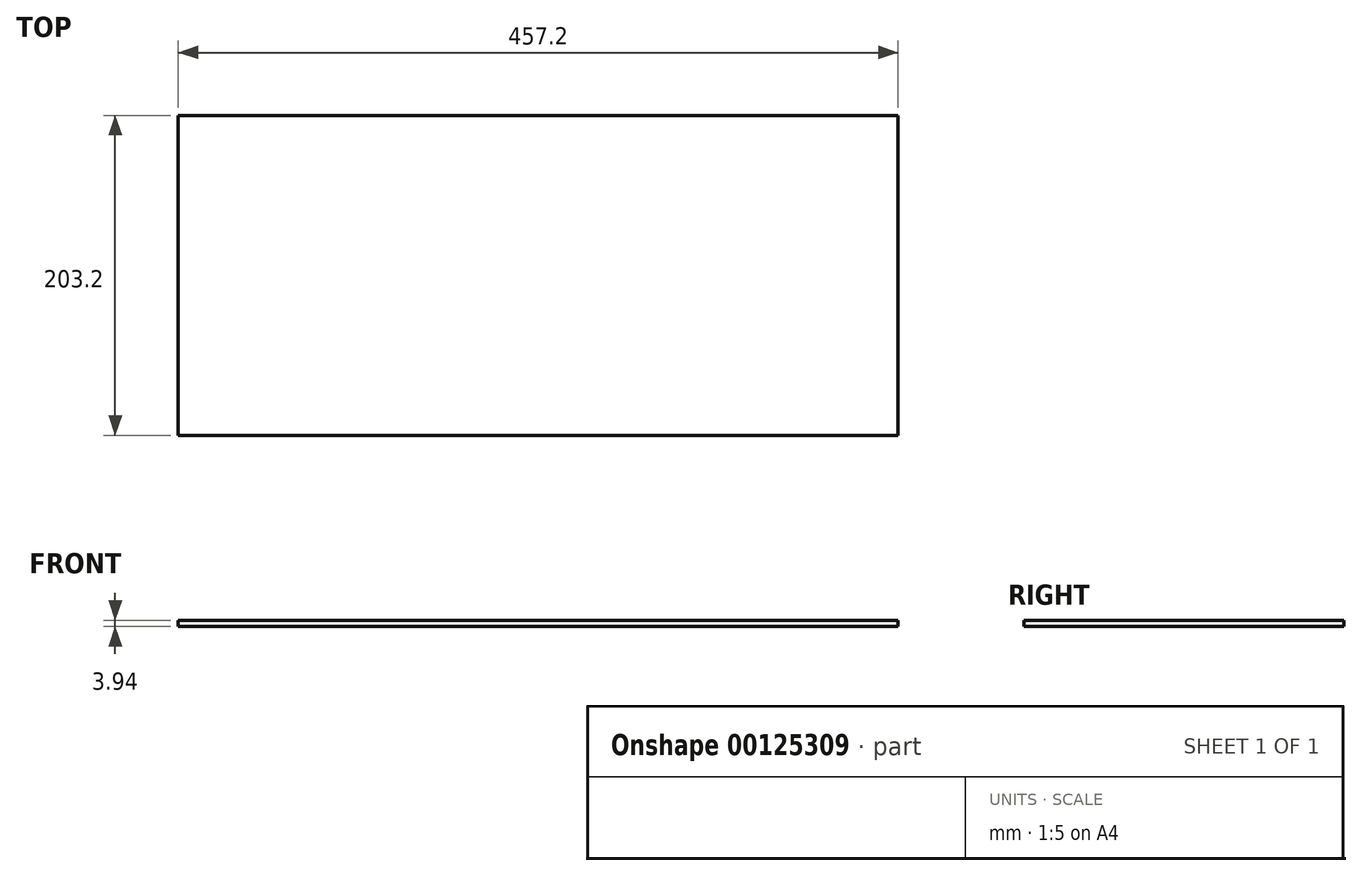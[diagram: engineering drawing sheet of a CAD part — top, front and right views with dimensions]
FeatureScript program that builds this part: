
annotation { "Feature Type Name" : "Feature", "Feature Type Description" : "" }
export const myFeature = defineFeature(function(context is Context, id is Id, definition is map)
    precondition{}
    {
        {
            var Q0;
            Q0=qCreatedBy(makeId("Top.planeOp"),FACE);
            var sketch = newSketch(context, id + "F0", { "sketchPlane" : qUnion([Q0])});
            skLineSegment(sketch, "E0.bottom", {"start": v(-228.6, -101.6) * mm, "end": v(228.6, -101.6) * mm});
            skLineSegment(sketch, "E0.top", {"start": v(-228.6, 101.6) * mm, "end": v(228.6, 101.6) * mm});
            skLineSegment(sketch, "E0.left", {"start": v(-228.6, -101.6) * mm, "end": v(-228.6, 101.6) * mm});
            skLineSegment(sketch, "E0.right", {"start": v(228.6, -101.6) * mm, "end": v(228.6, 101.6) * mm});
            skPoint(sketch, "E0.middle", {"position": v(0, 0) * mm});
            skSolve(sketch);
        }
        {
            var Q0;
            Q0 = qSketchRegion(id + "F0", true);
            extrude(context, id + "F1", {"entities" : qUnion([Q0]), "depth" : 3.94 * mm});
        }
    });
